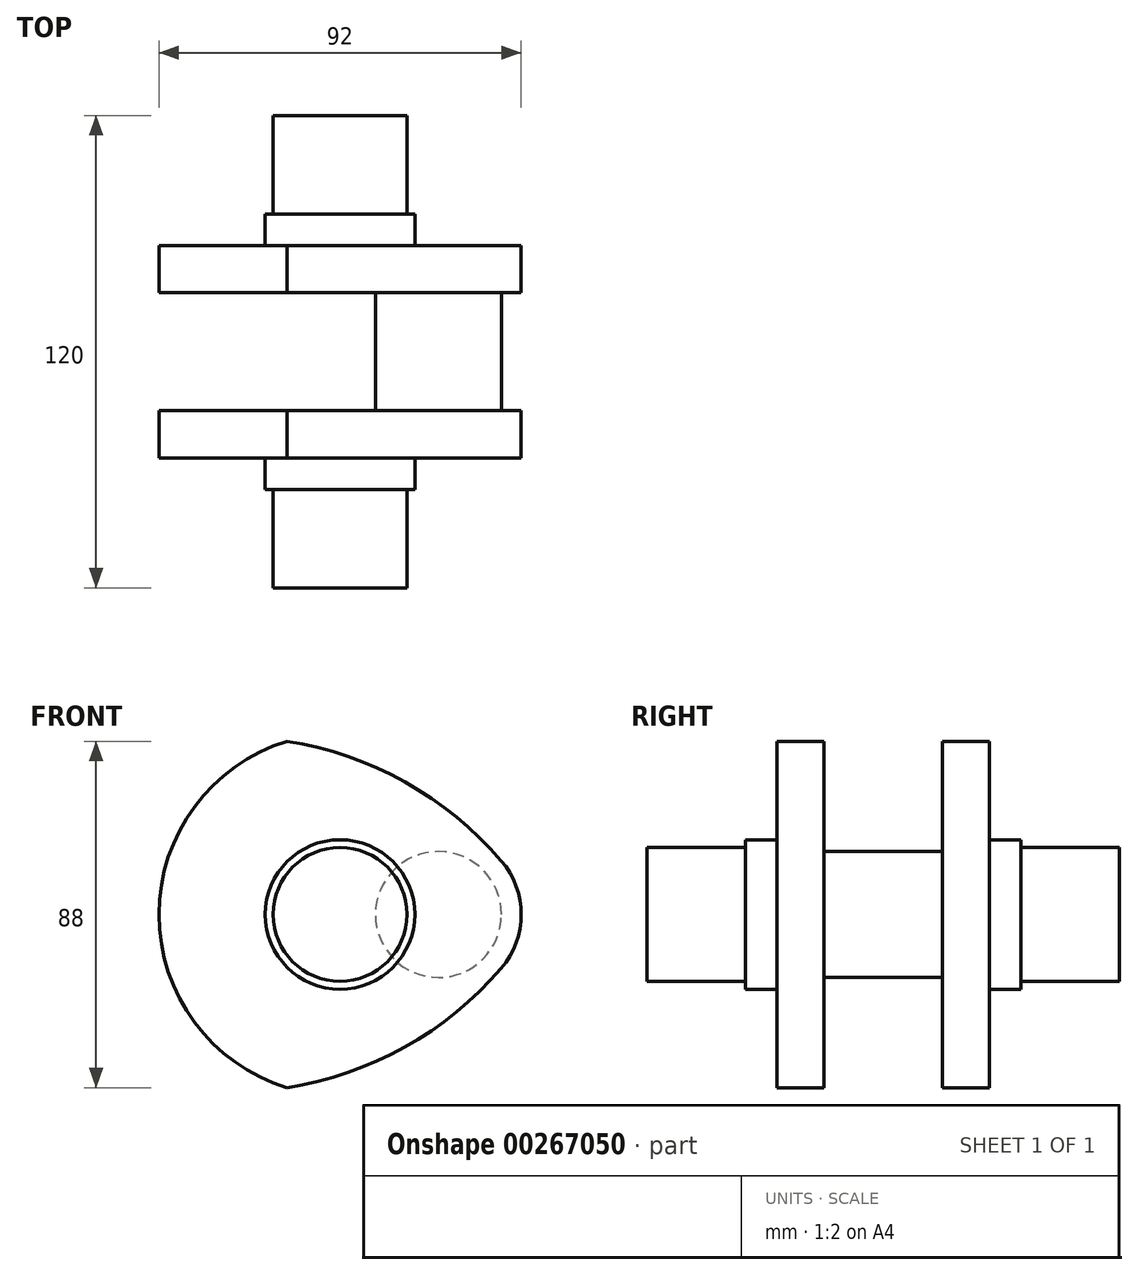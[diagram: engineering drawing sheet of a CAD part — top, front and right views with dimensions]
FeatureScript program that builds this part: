
annotation { "Feature Type Name" : "Feature", "Feature Type Description" : "" }
export const myFeature = defineFeature(function(context is Context, id is Id, definition is map)
    precondition{}
    {
        {
            var Q0;
            Q0=qCreatedBy(makeId("Front.planeOp"),FACE);
            var sketch = newSketch(context, id + "F0", { "sketchPlane" : qUnion([Q0])});
            skCircle(sketch, "E0", {"center": v(0, 0) * mm, "radius": 17 * mm});
            skSolve(sketch);
        }
        {
            var Q0;
            Q0 = qSketchRegion(id + "F0", true);
            extrude(context, id + "F1", {"entities" : qUnion([Q0]), "depth" : 25 * mm});
        }
        {
            var Q0;
            Q0=qCreatedBy(makeId("Front.planeOp"),FACE);
            var sketch = newSketch(context, id + "F2", { "sketchPlane" : qUnion([Q0])});
            skCircle(sketch, "E1", {"center": v(0, 0) * mm, "radius": 19 * mm});
            skSolve(sketch);
        }
        {
            var Q0;
            Q0 = qSketchRegion(id + "F2", true);
            extrude(context, id + "F3", {"entities" : qUnion([Q0]), "operationType" : NewBodyOperationType.ADD, "oppositeDirection" : true, "depth" : 8 * mm});
        }
        {
            var Q0;
            Q0=makeQuery(id+"F3.opExtrude","CAP_FACE",FACE,{"disambiguationData":[OSD([sQuery(id+"F2.wireOp",EDGE,"E1")])],"isStart":false});
            var sketch = newSketch(context, id + "F4", { "sketchPlane" : qUnion([Q0])});
            skArc(sketch, "E2", {"start": v(13.42, -44) * mm, "mid": v(46, 0) * mm, "end": v(13.42, 44) * mm});
            skLineSegment(sketch, "E3", {"start": v(13.42, -66.21) * mm, "end": v(13.42, 85.2) * mm, "construction": true});
            skArc(sketch, "E4", {"start": v(-40.94, 13.67) * mm, "mid": v(-46, 0) * mm, "end": v(-40.94, -13.67) * mm});
            skArc(sketch, "E5", {"start": v(-40.94, -13.67) * mm, "mid": v(-16.47, -33.68) * mm, "end": v(13.42, -44) * mm});
            skArc(sketch, "E6", {"start": v(13.42, 44) * mm, "mid": v(-16.47, 33.68) * mm, "end": v(-40.94, 13.67) * mm});
            skSolve(sketch);
        }
        {
            var Q0;
            Q0 = qSketchRegion(id + "F4", true);
            extrude(context, id + "F5", {"entities" : qUnion([Q0]), "operationType" : NewBodyOperationType.ADD, "depth" : 12 * mm});
        }
        {
            var Q0;
            Q0=makeQuery(id+"F5.opExtrude","CAP_FACE",FACE,{"disambiguationData":[OSD([sQuery(id+"F4.wireOp",EDGE,"E2"),sQuery(id+"F4.wireOp",EDGE,"E4"),sQuery(id+"F4.wireOp",EDGE,"E5"),sQuery(id+"F4.wireOp",EDGE,"E6")])],"isStart":false});
            var sketch = newSketch(context, id + "F6", { "sketchPlane" : qUnion([Q0])});
            skCircle(sketch, "E7", {"center": v(-25, 0) * mm, "radius": 16 * mm});
            skSolve(sketch);
        }
        {
            var Q0;
            Q0=makeQuery(id+"F6.imprint","IMPRINT",FACE,{"disambiguationData":[TD([[makeQuery(id+"F6.imprint","IMPRINT",EDGE,{"derivedFrom":sQuery(id+"F6.wireOp",EDGE,"E7")}),1.0]])]});
            extrude(context, id + "F7", {"entities" : qUnion([Q0]), "operationType" : NewBodyOperationType.ADD, "depth" : 15 * mm});
        }
        {
            var Q0;
            Q0=makeQuery(id+"F1.opExtrude","SWEPT_BODY",BODY,{"disambiguationData":[OSD([sQuery(id+"F0.wireOp",EDGE,"E0")])]});
            var Q1;
            Q1=makeQuery(id+"F7.opExtrude","CAP_FACE",FACE,{"disambiguationData":[OSD([sQuery(id+"F6.wireOp",EDGE,"E7")])],"isStart":false});
            mirror(context, id + "F8", {"operationType" : NewBodyOperationType.ADD, "entities" : qUnion([Q0]), "mirrorPlane" : qUnion([Q1])});
        }
    });
